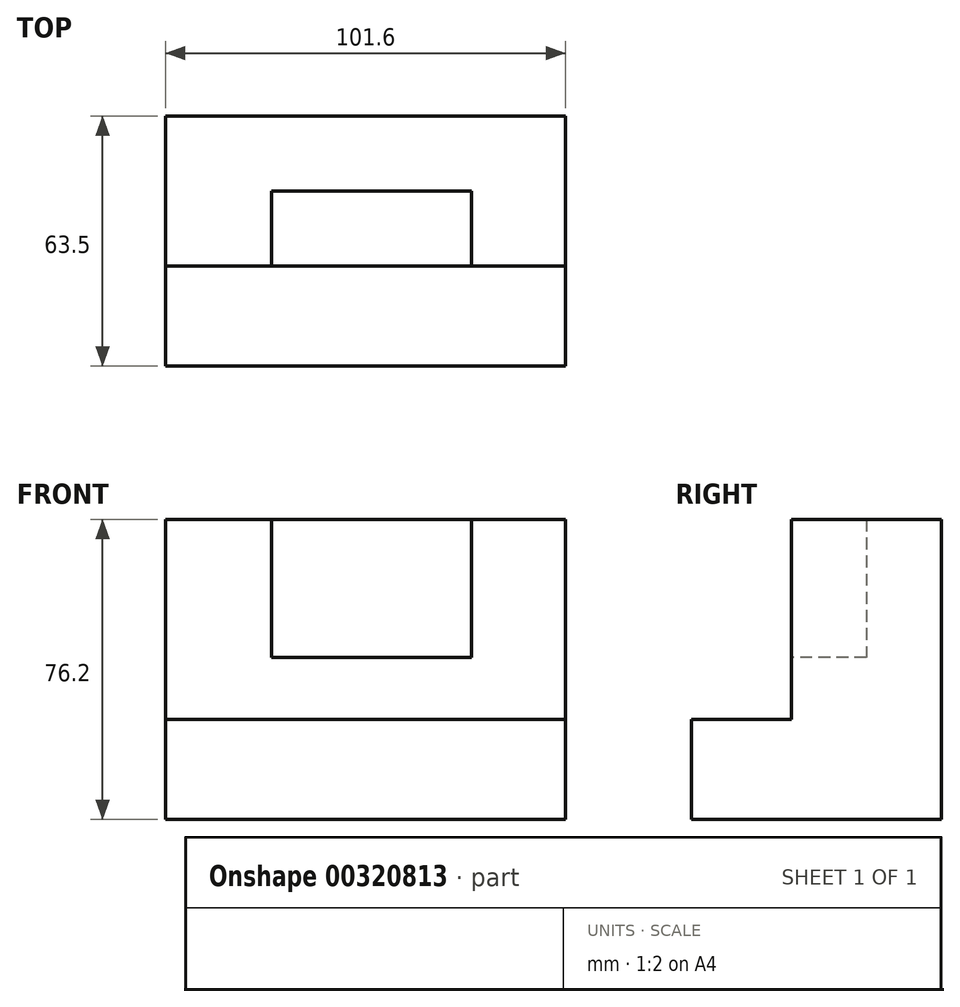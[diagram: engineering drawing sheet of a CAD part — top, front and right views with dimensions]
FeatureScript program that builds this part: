
annotation { "Feature Type Name" : "Feature", "Feature Type Description" : "" }
export const myFeature = defineFeature(function(context is Context, id is Id, definition is map)
    precondition{}
    {
        {
            var Q0;
            Q0=qCreatedBy(makeId("Right.planeOp"),FACE);
            var sketch = newSketch(context, id + "F0", { "sketchPlane" : qUnion([Q0])});
            skLineSegment(sketch, "E0", {"start": v(-30.58, -33.4) * mm, "end": v(32.92, -33.4) * mm});
            skLineSegment(sketch, "E1", {"start": v(32.92, -33.4) * mm, "end": v(32.92, 42.8) * mm});
            skLineSegment(sketch, "E2", {"start": v(32.92, 42.8) * mm, "end": v(-5.18, 42.8) * mm});
            skLineSegment(sketch, "E3", {"start": v(-5.18, 42.8) * mm, "end": v(-5.18, -8) * mm});
            skLineSegment(sketch, "E4", {"start": v(-5.18, -8) * mm, "end": v(-30.58, -8) * mm});
            skLineSegment(sketch, "E5", {"start": v(-30.58, -8) * mm, "end": v(-30.58, -33.4) * mm});
            skSolve(sketch);
        }
        {
            var Q0;
            Q0=makeQuery(id+"F0.imprint","IMPRINT",FACE,{"disambiguationData":[TD([[makeQuery(id+"F0.imprint","IMPRINT",EDGE,{"derivedFrom":sQuery(id+"F0.wireOp",EDGE,"E0")}),1.0]])]});
            extrude(context, id + "F1", {"entities" : qUnion([Q0]), "oppositeDirection" : true, "depth" : 101.6 * mm});
        }
        {
            var Q0;
            Q0=makeQuery(id+"F1.opExtrude","SWEPT_FACE",FACE,{"disambiguationData":[OSD([sQuery(id+"F0.wireOp",EDGE,"E3")])]});
            var sketch = newSketch(context, id + "F2", { "sketchPlane" : qUnion([Q0])});
            skLineSegment(sketch, "E6", {"start": v(-74.65, 42.8) * mm, "end": v(-74.65, 7.76) * mm});
            skLineSegment(sketch, "E7", {"start": v(-74.65, 7.76) * mm, "end": v(-23.85, 7.76) * mm});
            skLineSegment(sketch, "E8", {"start": v(-23.85, 7.76) * mm, "end": v(-23.85, 42.8) * mm});
            skLineSegment(sketch, "E9", {"start": v(-23.85, 42.8) * mm, "end": v(-74.65, 42.8) * mm});
            skLineSegment(sketch, "E10", {"start": v(-74.65, 42.8) * mm, "end": v(-23.85, 42.8) * mm});
            skSolve(sketch);
        }
        {
            var Q0;
            Q0=makeQuery(id+"F2.imprint","IMPRINT",FACE,{"disambiguationData":[TD([[makeQuery(id+"F2.imprint","IMPRINT",EDGE,{"derivedFrom":sQuery(id+"F2.wireOp",EDGE,"E6")}),1.0]])]});
            extrude(context, id + "F3", {"entities" : qUnion([Q0]), "operationType" : NewBodyOperationType.REMOVE, "oppositeDirection" : true, "depth" : 19.05 * mm});
        }
    });
